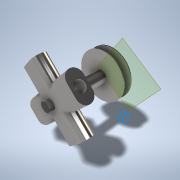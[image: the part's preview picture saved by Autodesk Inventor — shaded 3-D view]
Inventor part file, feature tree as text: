
AUTODESK INVENTOR PART (.ipt)
format: ipt  version: 2021 (Build 250183000, 183)  size: 246,784 bytes
history: native  units: mm
features: extrude x9, sketch x8, other x4, chamfer x2, projected_geometry x2, fillet x1, reference x1
ambient origin geometry x8: Origin, YZ Plane, XZ Plane, XY Plane, X Axis, Y Axis, Z Axis, Center Point
bodies: Body1 (feature_tree)
feature tree (27):
  other  "Bryła1"
  other  "Płaszczyzna konstrukcyjna1"
  extrude  "Wyciągnięcie proste1"  Depth=25.0mm
  extrude  "Wyciągnięcie proste2"  Depth=20.0mm TaperAngle=0.0deg
  chamfer  "Faza1"  Distance=100.0mm
  extrude  "Wyciągnięcie proste3"  Depth=10.0mm TaperAngle=0.0deg
  chamfer  "Faza2"  Distance=37.0mm Angle=45.0deg
  extrude  "Wyciągnięcie proste4"  Depth=100.0mm
  extrude  "Wyciągnięcie proste5"  Depth=10.0mm TaperAngle=0.0deg
  extrude  "Wyciągnięcie proste6"  Depth=37.0mm TaperAngle=45.0deg
  extrude  "Wyciągnięcie proste7"  Depth=150.0mm
  extrude  "Wyciągnięcie proste8"  Depth=30.0mm TaperAngle=0.0deg
  fillet  "Zaokrąglenie1"  Radius=140.0mm
  extrude  "Wyciągnięcie proste9"  TaperAngle=45.0deg  [1 undecoded]
  reference  "Odniesienie1"
  sketch  "Szkic2"
  sketch  "Szkic3"
  sketch  "Szkic4"
  sketch  "Szkic5"
  sketch  "Szkic6"
  sketch  "Szkic7"
  projected_geometry  "Pętla rzutowana1"
  sketch  "Szkic8"
  projected_geometry  "Pętla rzutowana2"
  sketch  "Szkic9"
  other  "cw12model.iam"
  other  "jakis_modulxD:1"
note: 1 required parameter value undecoded (feature->parameter linkage not recoverable at this tier; creation-order binding heuristic only, values carry confidence <= 0.55)
